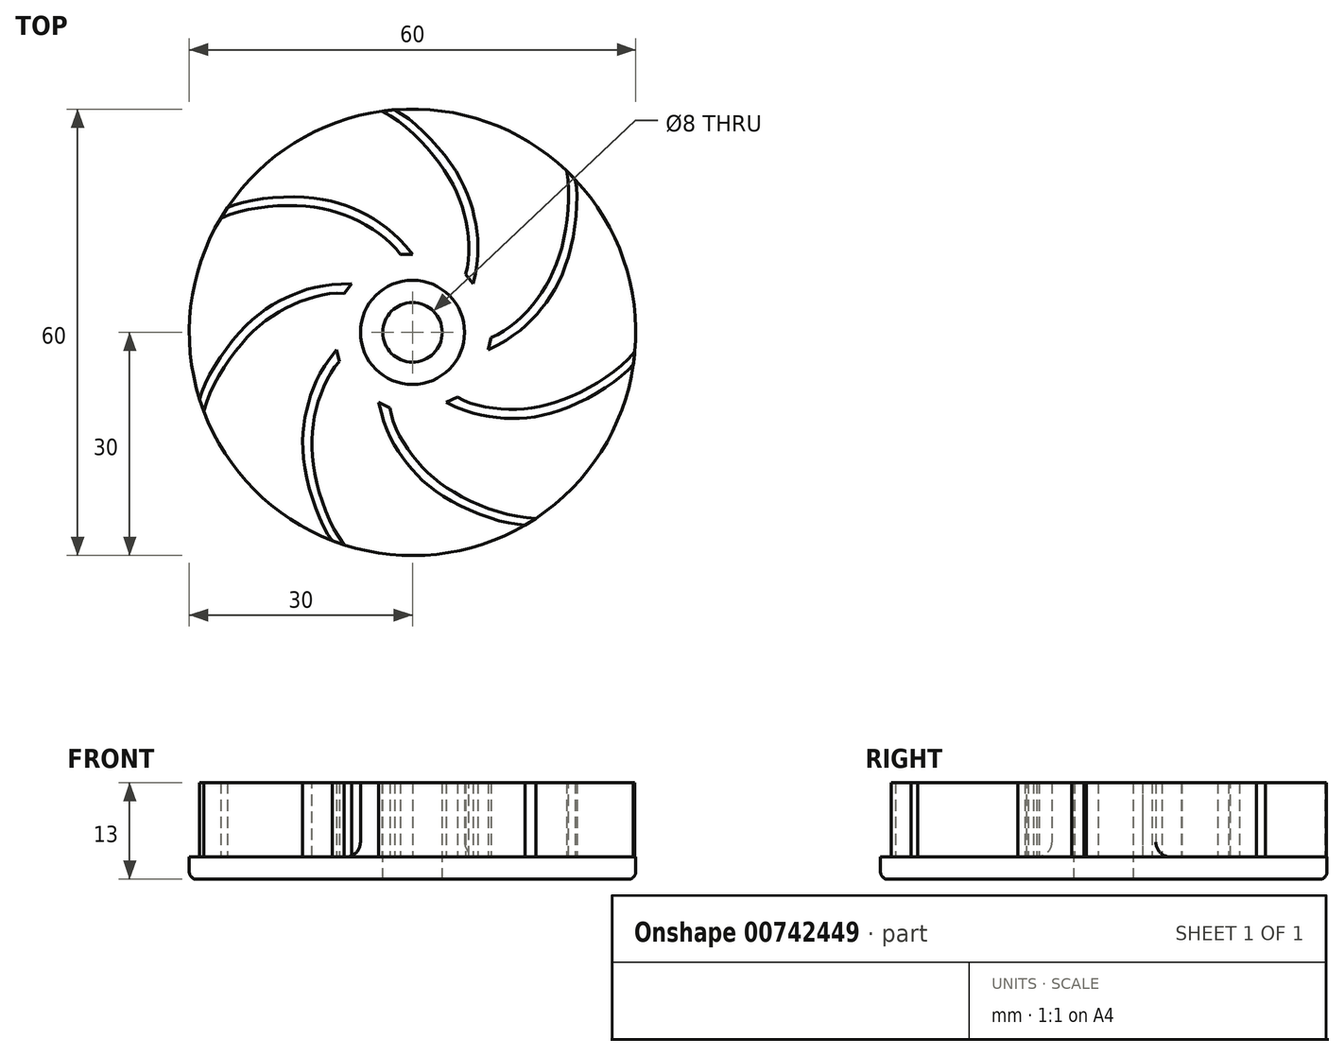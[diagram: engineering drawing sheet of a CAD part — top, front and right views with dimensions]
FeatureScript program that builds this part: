
annotation { "Feature Type Name" : "Feature", "Feature Type Description" : "" }
export const myFeature = defineFeature(function(context is Context, id is Id, definition is map)
    precondition{}
    {
        {
            var Q0;
            Q0=qCreatedBy(makeId("Top.planeOp"),FACE);
            var sketch = newSketch(context, id + "F0", { "sketchPlane" : qUnion([Q0])});
            skCircle(sketch, "E0", {"center": v(0, 0) * mm, "radius": 30 * mm});
            skSolve(sketch);
        }
        {
            var Q0;
            Q0=makeQuery(id+"F0.imprint","IMPRINT",FACE,{"disambiguationData":[TD([[makeQuery(id+"F0.imprint","IMPRINT",EDGE,{"derivedFrom":sQuery(id+"F0.wireOp",EDGE,"E0")}),1.0]])]});
            extrude(context, id + "F1", {"entities" : qUnion([Q0]), "depth" : 3 * mm, "offsetDistance" : 25 * mm});
        }
        {
            var Q0;
            Q0=makeQuery(id+"F1.opExtrude","CAP_FACE",FACE,{"disambiguationData":[OSD([sQuery(id+"F0.wireOp",EDGE,"E0")])],"isStart":false});
            var sketch = newSketch(context, id + "F2", { "sketchPlane" : qUnion([Q0])});
            skFitSpline(sketch, "E1", {"points": [v(0, 10.45) * mm, v(-6.46, 15.93) * mm, v(-13.98, 18.12) * mm, v(-24.88, 16.76) * mm], "startDerivative": vector(-20.73, 26.86) * mm, "endDerivative": vector(-20.88, -9.42) * mm});
            skFitSpline(sketch, "E2", {"points": [v(-1.64, 10.46) * mm, v(-7.1, 14.88) * mm, v(-14.6, 16.96) * mm, v(-25.79, 15.33) * mm], "startDerivative": vector(-11.92, 17.7) * mm, "endDerivative": vector(-26.26, -11.65) * mm});
            skLineSegment(sketch, "E3", {"start": v(-25.79, 15.33) * mm, "end": v(-24.88, 16.76) * mm});
            skLineSegment(sketch, "E4", {"start": v(-1.64, 10.46) * mm, "end": v(0, 10.45) * mm});
            skSolve(sketch);
        }
        {
            var Q0;
            Q0=qSketchRegion(id+"F2",true);
            extrude(context, id + "F3", {"entities" : qUnion([Q0]), "operationType" : NewBodyOperationType.ADD, "depth" : 10 * mm, "offsetDistance" : 25 * mm});
        }
        {
            var Q0;
            Q0=qCreatedBy(makeId("Front.planeOp"),FACE);
            var sketch = newSketch(context, id + "F4", { "sketchPlane" : qUnion([Q0])});
            skLineSegment(sketch, "E5", {"start": v(0, 0) * mm, "end": v(0, 45.71) * mm, "construction": true});
            skSolve(sketch);
        }
        {
            var Q0;
            Q0=makeQuery(id+"F1.opExtrude","SWEPT_BODY",BODY,{"disambiguationData":[OSD([sQuery(id+"F0.wireOp",EDGE,"E0")])]});
            var Q1;
            Q1=sQuery(id+"F4.wireOp",EDGE,"E5");
            circularPattern(context, id + "F5", {"entities" : qUnion([Q0]), "axis" : qUnion([Q1]), "angle" : 360 * degree, "instanceCount" : 7, "equalSpace" : true});
        }
        {
            var Q0;
            Q0=makeQuery(id+"F5.opPattern","COPY",FACE,{"derivedFrom":makeQuery(id+"F1.opExtrude","CAP_FACE",FACE,{"disambiguationData":[OSD([sQuery(id+"F0.wireOp",EDGE,"E0")])],"isStart":false}),"instanceName":"1"});
            var sketch = newSketch(context, id + "F6", { "sketchPlane" : qUnion([Q0])});
            skCircle(sketch, "E6", {"center": v(0, 0) * mm, "radius": 7 * mm});
            skSolve(sketch);
        }
        {
            var Q0;
            Q0=qSketchRegion(id+"F6",true);
            var Q1;
            Q1=sQuery(id+"F6.wireOp",EDGE,"E6");
            extrude(context, id + "F7", {"entities" : qUnion([Q0]), "operationType" : NewBodyOperationType.ADD, "surfaceEntities" : qUnion([Q1]), "depth" : 10 * mm, "offsetDistance" : 25 * mm});
        }
        {
            var Q0;
            Q0=makeQuery(id+"F7.opExtrude","CAP_FACE",FACE,{"disambiguationData":[OSD([sQuery(id+"F6.wireOp",EDGE,"E6")])],"isStart":false});
            var sketch = newSketch(context, id + "F8", { "sketchPlane" : qUnion([Q0])});
            skCircle(sketch, "E7", {"center": v(0, 0) * mm, "radius": 4 * mm});
            skSolve(sketch);
        }
        {
            var Q0;
            Q0=makeQuery(id+"F8.imprint","IMPRINT",FACE,{"disambiguationData":[TD([[makeQuery(id+"F8.imprint","IMPRINT",EDGE,{"derivedFrom":sQuery(id+"F8.wireOp",EDGE,"E7")}),1.0]])]});
            extrude(context, id + "F9", {"entities" : qUnion([Q0]), "operationType" : NewBodyOperationType.REMOVE, "endBound" : BoundingType.THROUGH_ALL, "oppositeDirection" : true, "depth" : 25 * mm, "offsetDistance" : 25 * mm});
        }
        {
            var Q0;
            Q0=makeQuery(id+"F1.opExtrude","CAP_EDGE",EDGE,{"disambiguationData":[OSD([sQuery(id+"F0.wireOp",EDGE,"E0")])],"isStart":true});
            fillet(context, id + "F10", {"entities" : qUnion([Q0]), "radius" : 1 * mm, "tangentPropagation" : true, "allowEdgeOverflow" : false});
        }
        {
            var Q0;
            {var subQ0=sQuery(id+"F0.wireOp",EDGE,"E0");var subQ1=makeQuery(id+"F1.opExtrude","CAP_FACE",FACE,{"disambiguationData":[OSD([subQ0])],"isStart":false});var subQ2=makeQuery(id+"F3.boolean.opBoolean","SPLIT",FACE,{"disambiguationData":[TD([makeQuery(id+"F1.opExtrude","SWEPT_FACE",FACE,{"disambiguationData":[OSD([subQ0])]}),subQ1,makeQuery(id+"F3.opExtrude","SWEPT_FACE",FACE,{"disambiguationData":[OSD([sQuery(id+"F2.wireOp",EDGE,"E1")])]}),makeQuery(id+"F3.opExtrude","SWEPT_FACE",FACE,{"disambiguationData":[OSD([sQuery(id+"F2.wireOp",EDGE,"E2")])]}),makeQuery(id+"F3.opExtrude","SWEPT_FACE",FACE,{"disambiguationData":[OSD([sQuery(id+"F2.wireOp",EDGE,"E3")])]}),makeQuery(id+"F3.opExtrude","SWEPT_FACE",FACE,{"disambiguationData":[OSD([sQuery(id+"F2.wireOp",EDGE,"E4")])]})])],"derivedFrom":subQ1});Q0=makeQuery(id+"F7.boolean.opBoolean","INTERSECT",EDGE,{"derivedFrom":[subQ2,makeQuery(id+"F5.opPattern","COPY",FACE,{"derivedFrom":subQ2,"instanceName":"1"}),makeQuery(id+"F5.opPattern","COPY",FACE,{"derivedFrom":subQ2,"instanceName":"2"}),makeQuery(id+"F5.opPattern","COPY",FACE,{"derivedFrom":subQ2,"instanceName":"3"}),makeQuery(id+"F5.opPattern","COPY",FACE,{"derivedFrom":subQ2,"instanceName":"4"}),makeQuery(id+"F5.opPattern","COPY",FACE,{"derivedFrom":subQ2,"instanceName":"5"}),makeQuery(id+"F5.opPattern","COPY",FACE,{"derivedFrom":subQ2,"instanceName":"6"})]});}
            fillet(context, id + "F11", {"entities" : qUnion([Q0]), "radius" : 2 * mm, "tangentPropagation" : true, "allowEdgeOverflow" : false});
        }
    });
